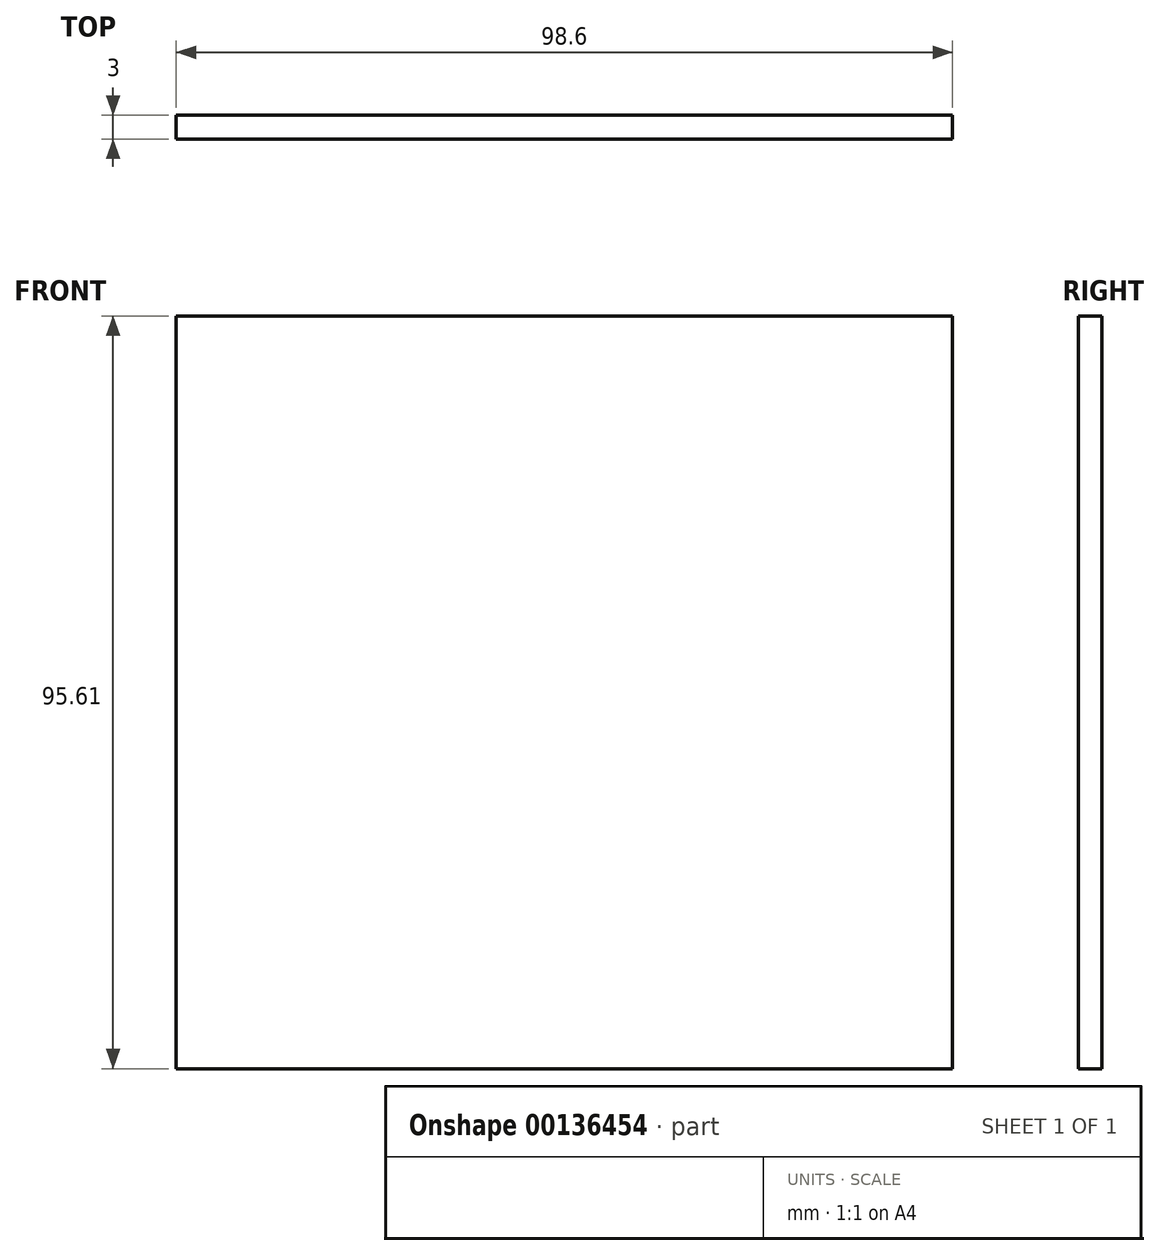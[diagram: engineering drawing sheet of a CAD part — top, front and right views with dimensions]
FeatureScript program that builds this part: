
annotation { "Feature Type Name" : "Feature", "Feature Type Description" : "" }
export const myFeature = defineFeature(function(context is Context, id is Id, definition is map)
    precondition{}
    {
        {
            var Q0;
            Q0=qCreatedBy(makeId("Front.planeOp"),FACE);
            var sketch = newSketch(context, id + "F0", { "sketchPlane" : qUnion([Q0])});
            skLineSegment(sketch, "E0.bottom", {"start": v(0, 0) * mm, "end": v(98.6, 0) * mm});
            skLineSegment(sketch, "E0.top", {"start": v(0, 95.6) * mm, "end": v(98.6, 95.6) * mm});
            skLineSegment(sketch, "E0.left", {"start": v(0, 0) * mm, "end": v(0, 95.6) * mm});
            skLineSegment(sketch, "E0.right", {"start": v(98.6, 0) * mm, "end": v(98.6, 95.6) * mm});
            skSolve(sketch);
        }
        {
            var Q0;
            Q0=makeQuery(id+"F0.imprint","IMPRINT",FACE,{"disambiguationData":[TD([[makeQuery(id+"F0.imprint","IMPRINT",EDGE,{"derivedFrom":sQuery(id+"F0.wireOp",EDGE,"E0.bottom")}),1.0]])]});
            extrude(context, id + "F1", {"entities" : qUnion([Q0]), "depth" : 3 * mm});
        }
    });
